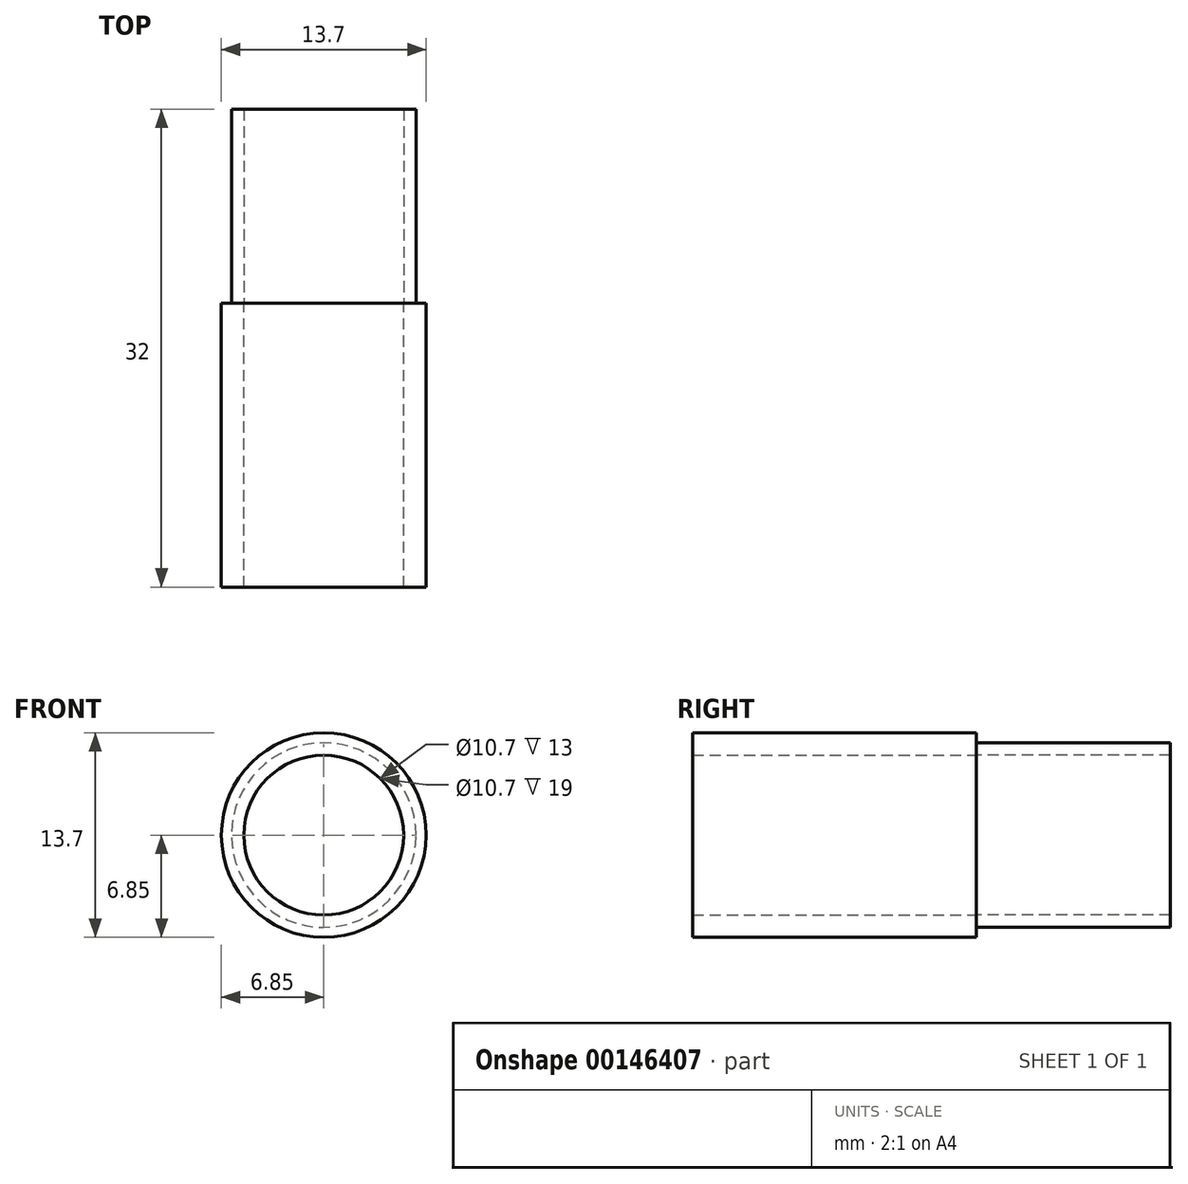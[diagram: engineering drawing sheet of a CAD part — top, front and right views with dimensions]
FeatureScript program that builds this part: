
annotation { "Feature Type Name" : "Feature", "Feature Type Description" : "" }
export const myFeature = defineFeature(function(context is Context, id is Id, definition is map)
    precondition{}
    {
        {
            assignVariable(context, id + "F0", {"name" : "Length1", "anyValue" : 19});
        }
        {
            assignVariable(context, id + "F1", {"name" : "Length2", "anyValue" : 13});
        }
        {
            var Q0;
            Q0=qCreatedBy(makeId("Front.planeOp"),FACE);
            var sketch = newSketch(context, id + "F2", { "sketchPlane" : qUnion([Q0])});
            skCircle(sketch, "E0", {"center": v(0, 0) * mm, "radius": 6.85 * mm});
            skCircle(sketch, "E1", {"center": v(0, 0) * mm, "radius": 4.76 * mm});
            skCircle(sketch, "E2", {"center": v(0, 0) * mm, "radius": 5.35 * mm});
            skSolve(sketch);
        }
        {
            var Q0;
            Q0=makeQuery(id+"F2.imprint","IMPRINT",FACE,{"disambiguationData":[TD([[makeQuery(id+"F2.imprint","IMPRINT",EDGE,{"derivedFrom":sQuery(id+"F2.wireOp",EDGE,"E0")}),1.0]])]});
            extrude(context, id + "F3", {"entities" : qUnion([Q0]), "depth" : (getVariable(context, 'Length1')) * mm});
        }
        {
            var Q0;
            Q0=qCreatedBy(makeId("Front.planeOp"),FACE);
            var sketch = newSketch(context, id + "F4", { "sketchPlane" : qUnion([Q0])});
            skCircle(sketch, "E3", {"center": v(0, 0) * mm, "radius": 5.35 * mm});
            skCircle(sketch, "E4", {"center": v(0, 0) * mm, "radius": 6.17 * mm});
            skSolve(sketch);
        }
        {
            var Q0;
            Q0=makeQuery(id+"F4.imprint","IMPRINT",FACE,{"disambiguationData":[TD([[makeQuery(id+"F4.imprint","IMPRINT",EDGE,{"derivedFrom":sQuery(id+"F4.wireOp",EDGE,"E3")}),-1.0]])]});
            extrude(context, id + "F5", {"entities" : qUnion([Q0]), "oppositeDirection" : true, "depth" : (getVariable(context, 'Length2')) * mm});
        }
    });
